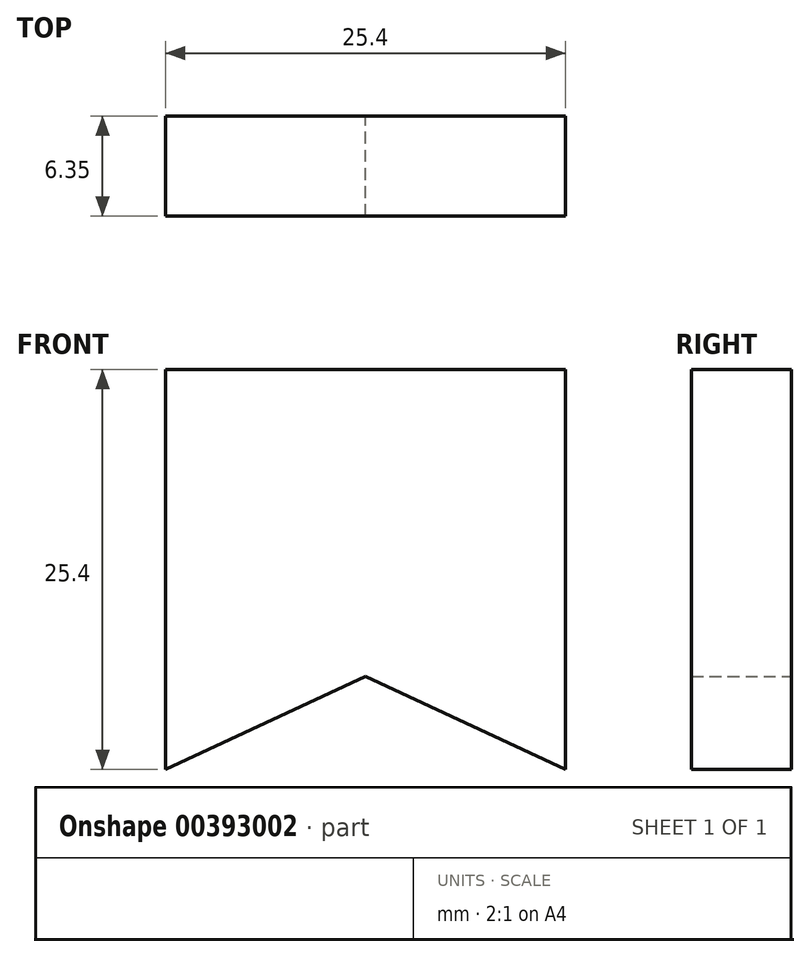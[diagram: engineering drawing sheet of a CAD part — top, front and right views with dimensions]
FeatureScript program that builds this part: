
annotation { "Feature Type Name" : "Feature", "Feature Type Description" : "" }
export const myFeature = defineFeature(function(context is Context, id is Id, definition is map)
    precondition{}
    {
        {
            var Q0;
            Q0=qCreatedBy(makeId("Front.planeOp"),FACE);
            var sketch = newSketch(context, id + "F0", { "sketchPlane" : qUnion([Q0])});
            skLineSegment(sketch, "E0", {"start": v(-12.7, 13.2) * mm, "end": v(-12.7, -12.2) * mm});
            skLineSegment(sketch, "E1", {"start": v(-12.7, 13.2) * mm, "end": v(12.7, 13.2) * mm});
            skLineSegment(sketch, "E2", {"start": v(12.7, 13.2) * mm, "end": v(12.7, -12.2) * mm});
            skLineSegment(sketch, "E3", {"start": v(12.7, -12.2) * mm, "end": v(0, -6.28) * mm});
            skLineSegment(sketch, "E4", {"start": v(0, -6.28) * mm, "end": v(-12.7, -12.2) * mm});
            skLineSegment(sketch, "E5", {"start": v(-12.7, -12.2) * mm, "end": v(12.7, -12.2) * mm, "construction": true});
            skSolve(sketch);
        }
        {
            var Q0;
            Q0 = qSketchRegion(id + "F0", true);
            extrude(context, id + "F1", {"entities" : qUnion([Q0]), "depth" : 6.35 * mm});
        }
    });
